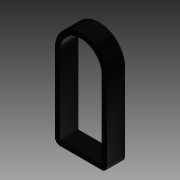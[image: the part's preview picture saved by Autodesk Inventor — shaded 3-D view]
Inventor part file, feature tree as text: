
AUTODESK INVENTOR PART (.ipt)
format: ipt  version: 2013 (Build 170138000, 138)  size: 90,112 bytes
history: native  units: in
note: dims shown in document units (in); Inventor stores cm internally (conversion verified against a paired STEP export)
features: reference x5, extrude x1, fillet x1, sketch x1
ambient origin geometry x8: Origin, YZ Plane, XZ Plane, XY Plane, X Axis, Y Axis, Z Axis, Center Point
bodies: Solid1 (feature_tree)
feature tree (8):
  extrude  "Extrusion1"  Depth=0.1378in TaperAngle=0.0deg
  fillet  "Fillet1"  Radius=0.0394in
  sketch  "Sketch1"  dims[d0=0.0394in d2=0.1378in d3=0.0in d4=0.0394in]
  reference  "Reference1"
  reference  "Reference2"
  reference  "Reference3"
  reference  "Reference4"
  reference  "Reference5"
